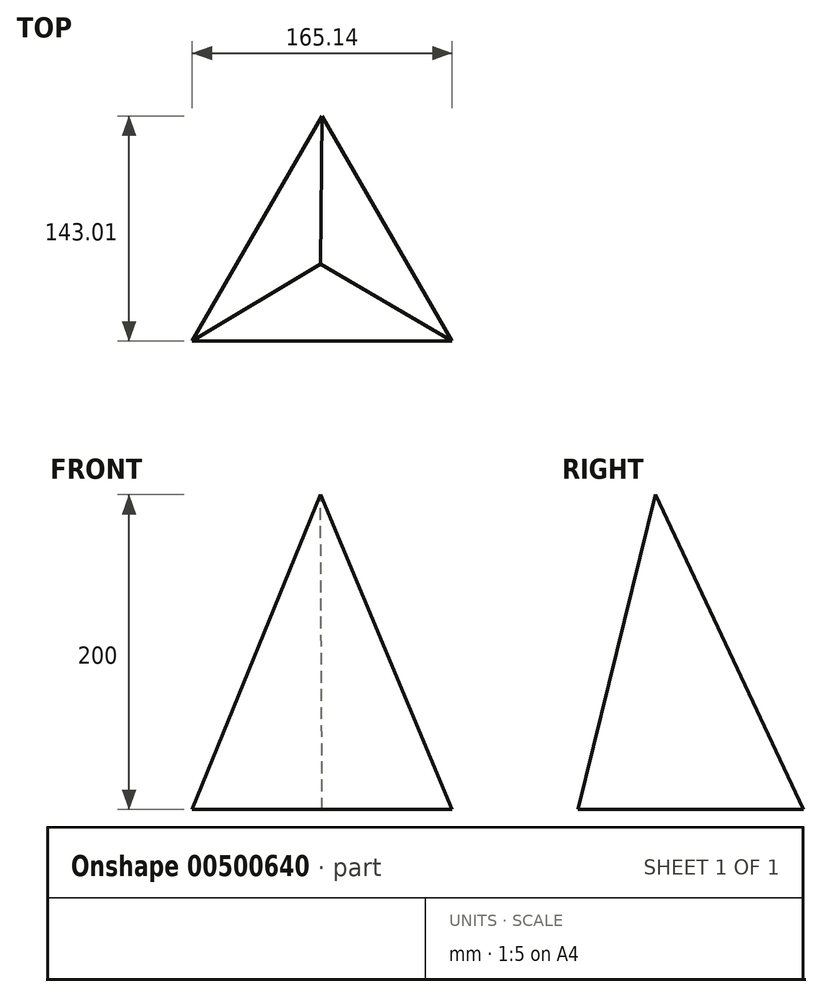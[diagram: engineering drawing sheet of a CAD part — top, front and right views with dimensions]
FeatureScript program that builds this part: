
annotation { "Feature Type Name" : "Feature", "Feature Type Description" : "" }
export const myFeature = defineFeature(function(context is Context, id is Id, definition is map)
    precondition{}
    {
        {
            var Q0;
            Q0=qCreatedBy(makeId("Top.planeOp"),FACE);
            var sketch = newSketch(context, id + "F0", { "sketchPlane" : qUnion([Q0])});
            skCircle(sketch, "E0.cCircle", {"center": v(0, 0) * mm, "radius": 95.34 * mm, "construction": true});
            skLineSegment(sketch, "E0.0", {"start": v(0, 95.34) * mm, "end": v(82.57, -47.67) * mm});
            skLineSegment(sketch, "E0.1", {"start": v(82.57, -47.67) * mm, "end": v(-82.57, -47.67) * mm});
            skLineSegment(sketch, "E0.2", {"start": v(-82.57, -47.67) * mm, "end": v(0, 95.34) * mm});
            skSolve(sketch);
        }
        {
            var Q0;
            Q0=qCreatedBy(makeId("Top.planeOp"),FACE);
            cPlane(context, id + "F1", {"entities" : qUnion([Q0]), "cplaneType" : CPlaneType.OFFSET, "offset" : 200 * mm, "width" : 150 * mm, "height" : 150 * mm});
        }
        {
            var Q0;
            Q0=qCreatedBy(id+"F1.planeOp",FACE);
            var sketch = newSketch(context, id + "F2", { "sketchPlane" : qUnion([Q0])});
            skPoint(sketch, "E1", {"position": v(-1, 1.34) * mm});
            skSolve(sketch);
        }
        {
            var Q0;
            Q0=makeQuery(id+"F0.imprint","IMPRINT",FACE,{"disambiguationData":[TD([[makeQuery(id+"F0.imprint","IMPRINT",EDGE,{"derivedFrom":sQuery(id+"F0.wireOp",EDGE,"E0.0")}),-1.0]])]});
            var Q1;
            Q1=sQuery(id+"F2.wireOp",VERTEX,"E1");
            loft(context, id + "F3", {"sheetProfilesArray" : [{ "sheetProfileEntities" : qUnion([Q0]) }, { "sheetProfileEntities" : qUnion([Q1]) }]});
        }
    });
